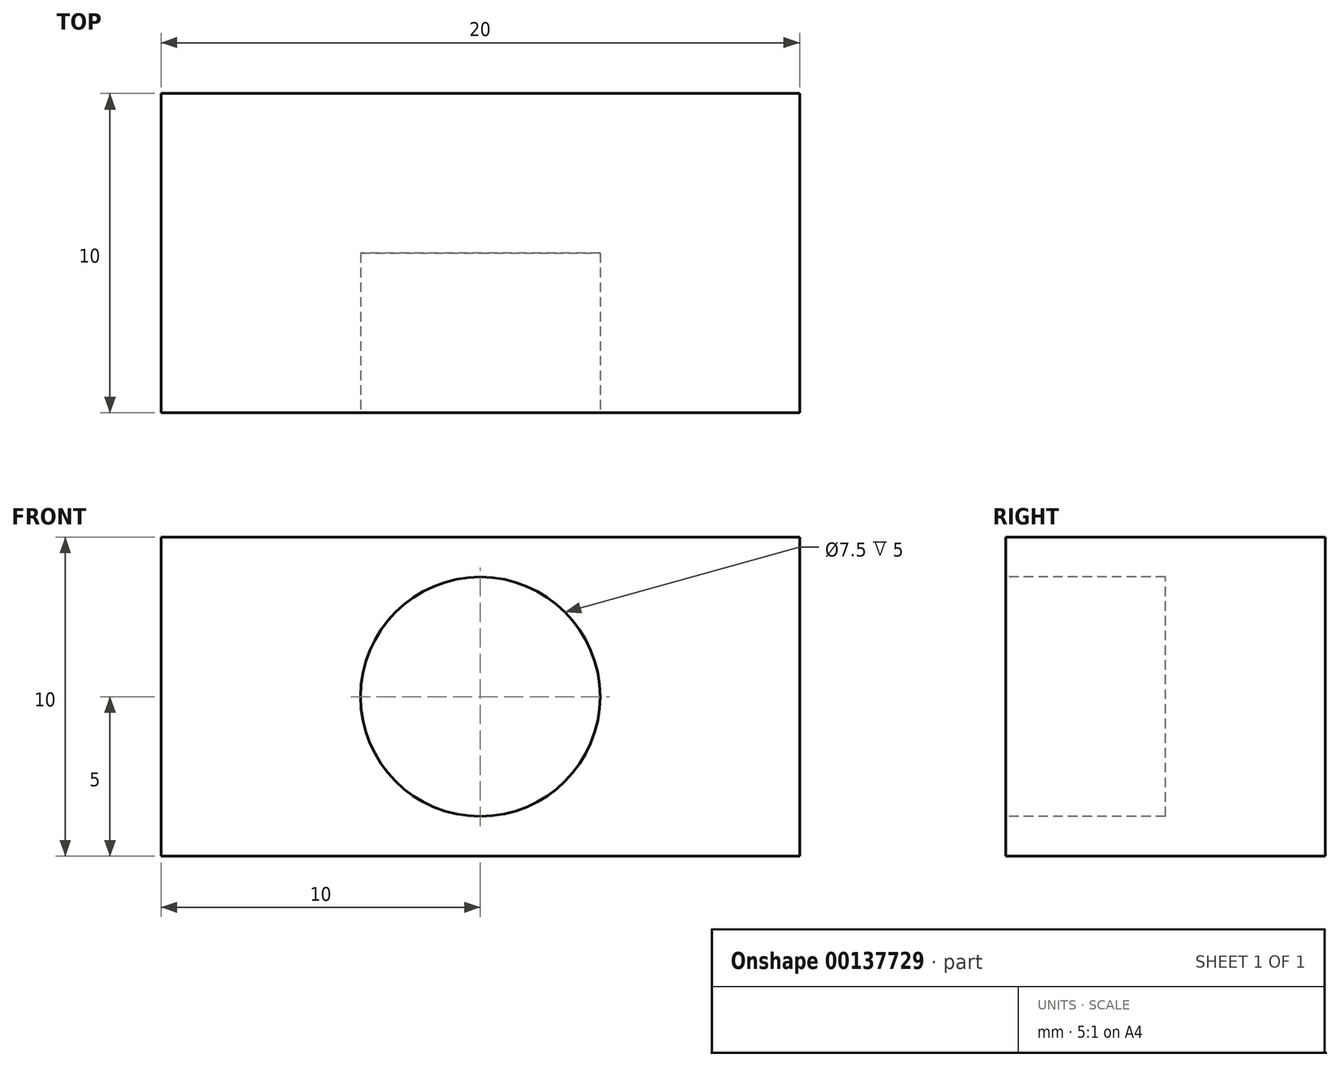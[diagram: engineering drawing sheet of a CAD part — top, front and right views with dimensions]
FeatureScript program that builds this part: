
annotation { "Feature Type Name" : "Feature", "Feature Type Description" : "" }
export const myFeature = defineFeature(function(context is Context, id is Id, definition is map)
    precondition{}
    {
        {
            var Q0;
            Q0=qCreatedBy(makeId("Front.planeOp"),FACE);
            var sketch = newSketch(context, id + "F0", { "sketchPlane" : qUnion([Q0])});
            skLineSegment(sketch, "E0.bottom", {"start": v(10, 5) * mm, "end": v(-10, 5) * mm});
            skLineSegment(sketch, "E0.top", {"start": v(10, -5) * mm, "end": v(-10, -5) * mm});
            skLineSegment(sketch, "E0.left", {"start": v(10, 5) * mm, "end": v(10, -5) * mm});
            skLineSegment(sketch, "E0.right", {"start": v(-10, 5) * mm, "end": v(-10, -5) * mm});
            skPoint(sketch, "E0.middle", {"position": v(0, 0) * mm});
            skSolve(sketch);
        }
        {
            var Q0;
            Q0=qSketchRegion(id+"F0",true);
            extrude(context, id + "F1", {"entities" : qUnion([Q0]), "depth" : 10 * mm});
        }
        {
            var Q0;
            Q0=makeQuery(id+"F1.opExtrude","CAP_FACE",FACE,{"disambiguationData":[OSD([sQuery(id+"F0.wireOp",EDGE,"E0.bottom"),sQuery(id+"F0.wireOp",EDGE,"E0.top"),sQuery(id+"F0.wireOp",EDGE,"E0.left"),sQuery(id+"F0.wireOp",EDGE,"E0.right")])],"isStart":false});
            var sketch = newSketch(context, id + "F2", { "sketchPlane" : qUnion([Q0])});
            skCircle(sketch, "E1", {"center": v(0, 0) * mm, "radius": 3.75 * mm});
            skSolve(sketch);
        }
        {
            var Q0;
            Q0=qSketchRegion(id+"F2",true);
            extrude(context, id + "F3", {"entities" : qUnion([Q0]), "operationType" : NewBodyOperationType.REMOVE, "oppositeDirection" : true, "depth" : 5 * mm});
        }
    });
